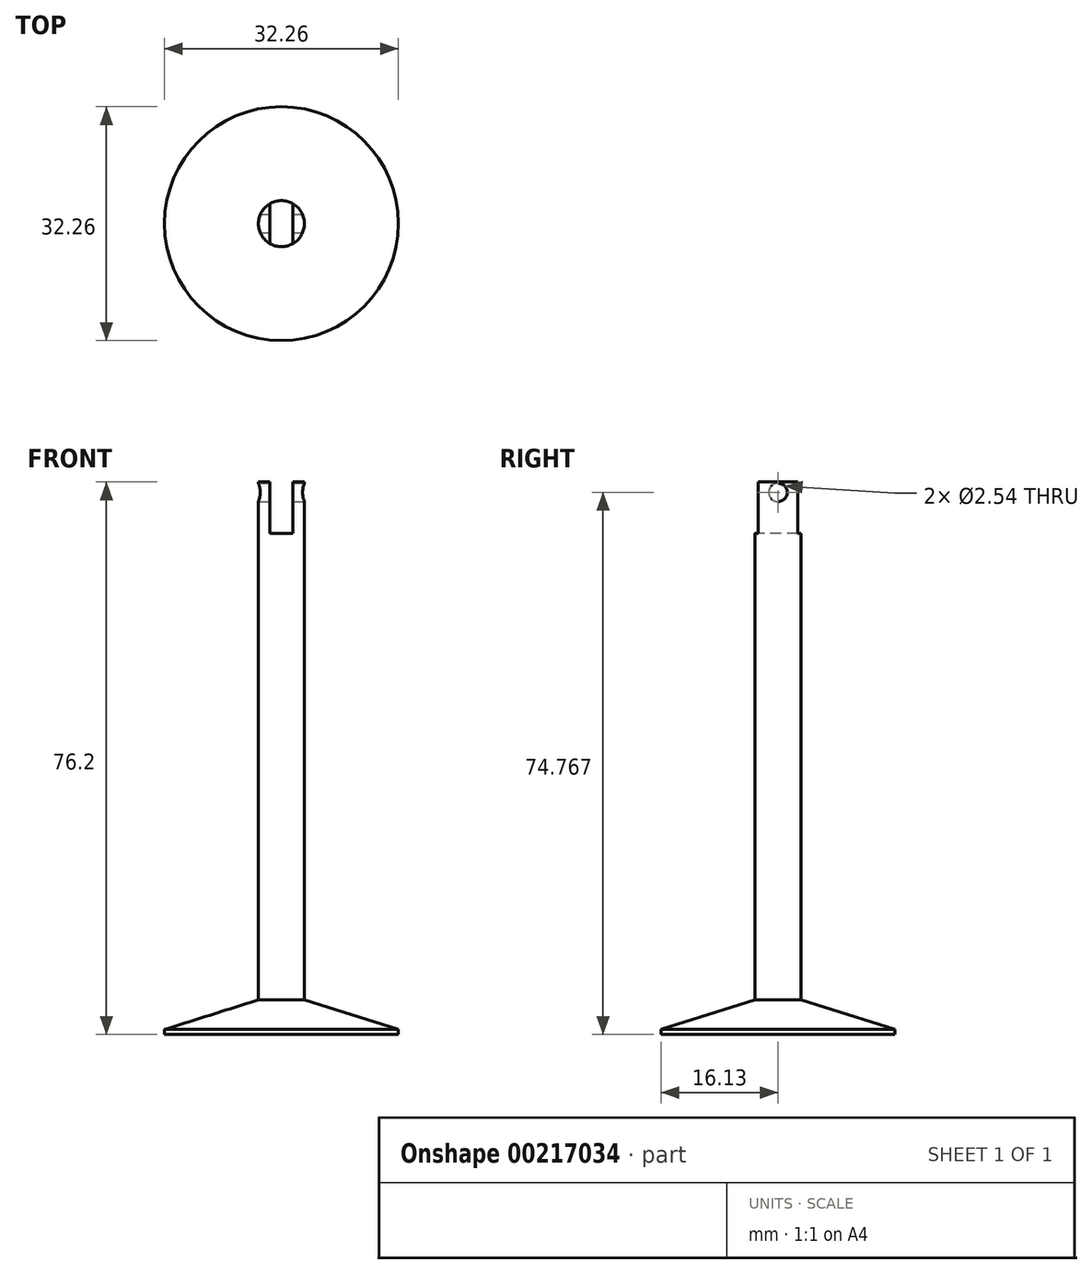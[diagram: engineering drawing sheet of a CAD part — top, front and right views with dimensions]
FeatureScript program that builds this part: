
annotation { "Feature Type Name" : "Feature", "Feature Type Description" : "" }
export const myFeature = defineFeature(function(context is Context, id is Id, definition is map)
    precondition{}
    {
        {
            var Q0;
            Q0=qCreatedBy(makeId("Top.planeOp"),FACE);
            var sketch = newSketch(context, id + "F0", { "sketchPlane" : qUnion([Q0])});
            skCircle(sketch, "E0", {"center": v(0, 0) * mm, "radius": 16.13 * mm});
            skSolve(sketch);
        }
        {
            var Q0;
            Q0=makeQuery(id+"F0.imprint","IMPRINT",FACE,{"disambiguationData":[TD([[makeQuery(id+"F0.imprint","IMPRINT",EDGE,{"derivedFrom":sQuery(id+"F0.wireOp",EDGE,"E0")}),1.0]])]});
            extrude(context, id + "F1", {"entities" : qUnion([Q0]), "depth" : 76.2 * mm});
        }
        {
            var Q0;
            Q0=qCreatedBy(makeId("Front.planeOp"),FACE);
            var sketch = newSketch(context, id + "F2", { "sketchPlane" : qUnion([Q0])});
            skLineSegment(sketch, "E1.bottom", {"start": v(3.17, 4.79) * mm, "end": v(-3.18, 4.79) * mm});
            skLineSegment(sketch, "E1.top", {"start": v(3.17, 149.2) * mm, "end": v(-3.18, 149.2) * mm});
            skLineSegment(sketch, "E1.left", {"start": v(3.17, 4.79) * mm, "end": v(3.17, 149.2) * mm});
            skLineSegment(sketch, "E1.right", {"start": v(-3.18, 4.79) * mm, "end": v(-3.18, 149.2) * mm});
            skPoint(sketch, "E1.middle", {"position": v(0, 77) * mm});
            skLineSegment(sketch, "E2", {"start": v(-3.18, 4.79) * mm, "end": v(-18.34, 0) * mm});
            skLineSegment(sketch, "E3", {"start": v(-18.34, 0) * mm, "end": v(-18.34, 89.8) * mm});
            skLineSegment(sketch, "E4", {"start": v(-18.34, 89.8) * mm, "end": v(-3.18, 89.8) * mm});
            skSolve(sketch);
        }
        {
            var Q0;
            {var subQ0=sQuery(id+"F2.wireOp",EDGE,"E2");Q0=makeQuery(id+"F2.imprint","IMPRINT",FACE,{"disambiguationData":[TD([[makeQuery(id+"F2.imprint","IMPRINT",EDGE,{"derivedFrom":subQ0}),-1.0]])]});}
            var Q1;
            Q1=makeQuery(id+"F1.opExtrude","CAP_EDGE",EDGE,{"disambiguationData":[OSD([sQuery(id+"F0.wireOp",EDGE,"E0")])],"isStart":false});
            revolve(context, id + "F3", {"operationType" : NewBodyOperationType.REMOVE, "entities" : qUnion([Q0]), "axis" : qUnion([Q1]), "revolveType" : RevolveType.FULL, "oppositeDirection" : true});
        }
        {
            var Q0;
            Q0=qCreatedBy(makeId("Front.planeOp"),FACE);
            var sketch = newSketch(context, id + "F4", { "sketchPlane" : qUnion([Q0])});
            skLineSegment(sketch, "E5.bottom", {"start": v(1.59, 71.64) * mm, "end": v(-1.59, 71.64) * mm});
            skLineSegment(sketch, "E5.top", {"start": v(1.59, 81.8) * mm, "end": v(-1.59, 81.8) * mm});
            skLineSegment(sketch, "E5.left", {"start": v(1.59, 71.64) * mm, "end": v(1.59, 81.8) * mm});
            skLineSegment(sketch, "E5.right", {"start": v(-1.59, 71.64) * mm, "end": v(-1.59, 81.8) * mm});
            skPoint(sketch, "E5.middle", {"position": v(0, 76.72) * mm});
            skSolve(sketch);
        }
        {
            var Q0;
            Q0 = qSketchRegion(id + "F4", true);
            extrude(context, id + "F5", {"entities" : qUnion([Q0]), "operationType" : NewBodyOperationType.REMOVE, "oppositeDirection" : true, "depth" : 25.4 * mm, "symmetric" : true});
        }
        {
            var Q0;
            Q0=qCreatedBy(makeId("Right.planeOp"),FACE);
            var sketch = newSketch(context, id + "F6", { "sketchPlane" : qUnion([Q0])});
            skCircle(sketch, "E6", {"center": v(0, 74.77) * mm, "radius": 1.27 * mm});
            skPoint(sketch, "E7.trimOffspring.end.orphan", {"position": v(0, 73.13) * mm});
            skPoint(sketch, "E8.start.orphan", {"position": v(0, 76.4) * mm});
            skSolve(sketch);
        }
        {
            var Q0;
            Q0=makeQuery(id+"F6.imprint","IMPRINT",FACE,{"disambiguationData":[TD([[makeQuery(id+"F6.imprint","IMPRINT",EDGE,{"derivedFrom":sQuery(id+"F6.wireOp",EDGE,"E6")}),1.0]])]});
            extrude(context, id + "F7", {"entities" : qUnion([Q0]), "operationType" : NewBodyOperationType.REMOVE, "oppositeDirection" : true, "depth" : 25.4 * mm, "symmetric" : true});
        }
        {
            var Q0;
            Q0=makeQuery(id+"F5.boolean.opBoolean","COPY",FACE,{"derivedFrom":makeQuery(id+"F5.opExtrude","SWEPT_FACE",FACE,{"disambiguationData":[OSD([sQuery(id+"F4.wireOp",EDGE,"E5.bottom")])]})});
            extrude(context, id + "F8", {"entities" : qUnion([Q0]), "operationType" : NewBodyOperationType.REMOVE, "oppositeDirection" : true, "depth" : 2.54 * mm});
        }
    });
